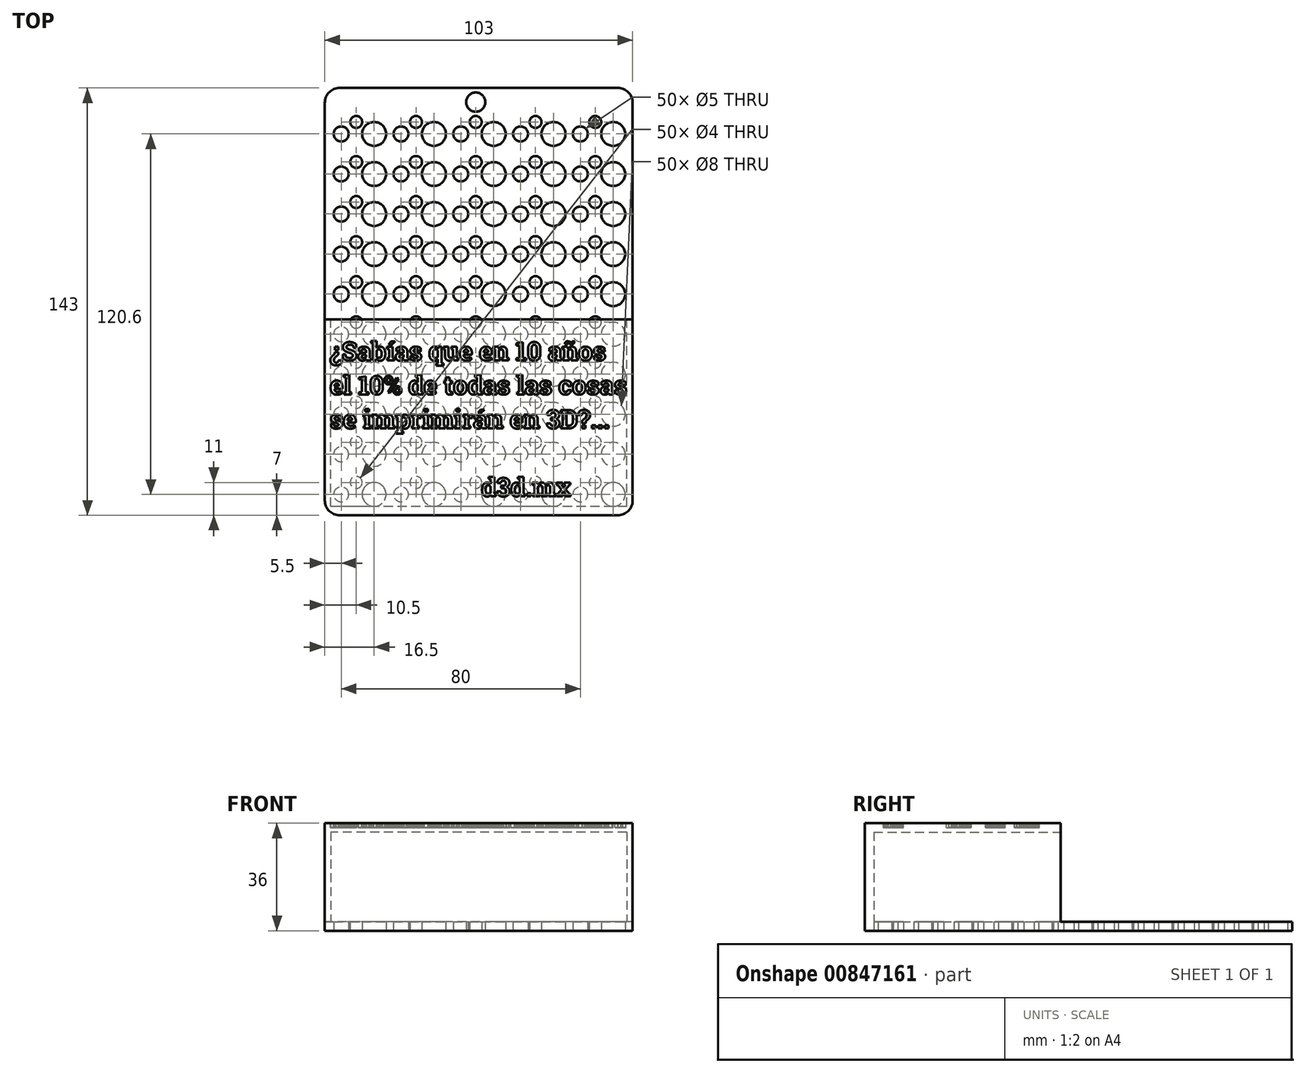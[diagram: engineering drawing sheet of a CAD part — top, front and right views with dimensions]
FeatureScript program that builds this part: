
annotation { "Feature Type Name" : "Feature", "Feature Type Description" : "" }
export const myFeature = defineFeature(function(context is Context, id is Id, definition is map)
    precondition{}
    {
        {
            var Q0;
            Q0=qCreatedBy(makeId("Top.planeOp"),FACE);
            var sketch = newSketch(context, id + "F0", { "sketchPlane" : qUnion([Q0])});
            skLineSegment(sketch, "E0.bottom", {"start": v(5, 0) * mm, "end": v(98, 0) * mm});
            skLineSegment(sketch, "E0.top", {"start": v(5, 143) * mm, "end": v(98, 143) * mm});
            skLineSegment(sketch, "E0.left", {"start": v(0, 5) * mm, "end": v(0, 138) * mm});
            skLineSegment(sketch, "E0.right", {"start": v(103, 5) * mm, "end": v(103, 138) * mm});
            skPoint(sketch, "E1.visualSharp", {"position": v(0, 143) * mm});
            skArc(sketch, "E1.filletArc", {"start": v(5, 143) * mm, "mid": v(1.46, 141.54) * mm, "end": v(0, 138) * mm});
            skPoint(sketch, "E2.visualSharp", {"position": v(103, 143) * mm});
            skArc(sketch, "E2.filletArc", {"start": v(103, 138) * mm, "mid": v(101.54, 141.54) * mm, "end": v(98, 143) * mm});
            skPoint(sketch, "E3.visualSharp", {"position": v(0, 0) * mm});
            skArc(sketch, "E3.filletArc", {"start": v(0, 5) * mm, "mid": v(1.46, 1.46) * mm, "end": v(5, 0) * mm});
            skPoint(sketch, "E4.visualSharp", {"position": v(103, 0) * mm});
            skArc(sketch, "E4.filletArc", {"start": v(98, 0) * mm, "mid": v(101.54, 1.46) * mm, "end": v(103, 5) * mm});
            skSolve(sketch);
        }
        {
            var Q0;
            Q0 = qSketchRegion(id + "F0", true);
            extrude(context, id + "F1", {"entities" : qUnion([Q0]), "depth" : 36 * mm, "offsetDistance" : 25 * mm});
        }
        {
            var Q0;
            Q0=makeQuery(id+"F1.opExtrude","SWEPT_FACE",FACE,{"disambiguationData":[OSD([sQuery(id+"F0.wireOp",EDGE,"E0.top")])]});
            var sketch = newSketch(context, id + "F2", { "sketchPlane" : qUnion([Q0])});
            skLineSegment(sketch, "E5.bottom", {"start": v(-103, 36) * mm, "end": v(0, 36) * mm});
            skLineSegment(sketch, "E5.top", {"start": v(-103, 3) * mm, "end": v(0, 3) * mm});
            skLineSegment(sketch, "E5.left", {"start": v(-103, 36) * mm, "end": v(-103, 3) * mm});
            skLineSegment(sketch, "E5.right", {"start": v(0, 36) * mm, "end": v(0, 3) * mm});
            skSolve(sketch);
        }
        {
            var Q0;
            Q0 = qSketchRegion(id + "F2", true);
            extrude(context, id + "F3", {"entities" : qUnion([Q0]), "operationType" : NewBodyOperationType.REMOVE, "oppositeDirection" : true, "depth" : 77.5 * mm, "offsetDistance" : 25 * mm});
        }
        {
            var Q0;
            Q0=makeQuery(id+"F3.boolean.opBoolean","COPY",FACE,{"derivedFrom":makeQuery(id+"F3.opExtrude","CAP_FACE",FACE,{"disambiguationData":[OSD([sQuery(id+"F2.wireOp",EDGE,"E5.bottom"),sQuery(id+"F2.wireOp",EDGE,"E5.top"),sQuery(id+"F2.wireOp",EDGE,"E5.left"),sQuery(id+"F2.wireOp",EDGE,"E5.right")])],"isStart":false})});
            var sketch = newSketch(context, id + "F4", { "sketchPlane" : qUnion([Q0])});
            skLineSegment(sketch, "E6.bottom", {"start": v(-101, 33) * mm, "end": v(-2, 33) * mm});
            skLineSegment(sketch, "E6.top", {"start": v(-101, 3) * mm, "end": v(-2, 3) * mm});
            skLineSegment(sketch, "E6.left", {"start": v(-101, 33) * mm, "end": v(-101, 3) * mm});
            skLineSegment(sketch, "E6.right", {"start": v(-2, 33) * mm, "end": v(-2, 3) * mm});
            skSolve(sketch);
        }
        {
            var Q0;
            Q0 = qSketchRegion(id + "F4", true);
            extrude(context, id + "F5", {"entities" : qUnion([Q0]), "operationType" : NewBodyOperationType.REMOVE, "oppositeDirection" : true, "depth" : 62.5 * mm, "offsetDistance" : 25 * mm});
        }
        {
            var Q0;
            Q0=makeQuery(id+"F1.opExtrude","CAP_FACE",FACE,{"disambiguationData":[OSD([sQuery(id+"F0.wireOp",EDGE,"E0.bottom"),sQuery(id+"F0.wireOp",EDGE,"E0.top"),sQuery(id+"F0.wireOp",EDGE,"E0.left"),sQuery(id+"F0.wireOp",EDGE,"E0.right"),sQuery(id+"F0.wireOp",EDGE,"E1.filletArc"),sQuery(id+"F0.wireOp",EDGE,"E2.filletArc"),sQuery(id+"F0.wireOp",EDGE,"E3.filletArc"),sQuery(id+"F0.wireOp",EDGE,"E4.filletArc")])],"isStart":false});
            var sketch = newSketch(context, id + "F6", { "sketchPlane" : qUnion([Q0])});
            skText(sketch, "E7", { "text": "¿Sabías que en 10 años\nel 10% de todas las cosas\nse imprimirán en 3D?...\n\n                        d3d.mx", "fontName": "RobotoSlab-Bold.ttf"});
            const initialGuessF6  = {"E7": [0.00164, 0.0518, 1, 0, 0.0062]};
            skSetInitialGuess(sketch, initialGuessF6);
            skSolve(sketch);
        }
        {
            var Q0;
            Q0 = qSketchRegion(id + "F6", true);
            extrude(context, id + "F7", {"entities" : qUnion([Q0]), "operationType" : NewBodyOperationType.REMOVE, "oppositeDirection" : true, "depth" : 1.5 * mm, "offsetDistance" : 25 * mm});
        }
        {
            var Q0;
            Q0=makeQuery(id+"F1.opExtrude","CAP_FACE",FACE,{"disambiguationData":[OSD([sQuery(id+"F0.wireOp",EDGE,"E0.bottom"),sQuery(id+"F0.wireOp",EDGE,"E0.top"),sQuery(id+"F0.wireOp",EDGE,"E0.left"),sQuery(id+"F0.wireOp",EDGE,"E0.right"),sQuery(id+"F0.wireOp",EDGE,"E1.filletArc"),sQuery(id+"F0.wireOp",EDGE,"E2.filletArc"),sQuery(id+"F0.wireOp",EDGE,"E3.filletArc"),sQuery(id+"F0.wireOp",EDGE,"E4.filletArc")])],"isStart":true});
            var sketch = newSketch(context, id + "F8", { "sketchPlane" : qUnion([Q0])});
            skCircle(sketch, "E8", {"center": v(5.5, -7) * mm, "radius": 2.5 * mm});
            skCircle(sketch, "E9", {"center": v(10.5, -11) * mm, "radius": 2 * mm});
            skCircle(sketch, "E10", {"center": v(16.5, -7) * mm, "radius": 4 * mm});
            skCircle(sketch, "E11.0.1.0", {"center": v(16.5, -20.4) * mm, "radius": 4 * mm});
            skCircle(sketch, "E11.0.1.1", {"center": v(10.5, -24.4) * mm, "radius": 2 * mm});
            skCircle(sketch, "E11.0.1.2", {"center": v(5.5, -20.4) * mm, "radius": 2.5 * mm});
            skCircle(sketch, "E11.0.2.0", {"center": v(16.5, -33.8) * mm, "radius": 4 * mm});
            skCircle(sketch, "E11.0.2.1", {"center": v(10.5, -37.8) * mm, "radius": 2 * mm});
            skCircle(sketch, "E11.0.2.2", {"center": v(5.5, -33.8) * mm, "radius": 2.5 * mm});
            skCircle(sketch, "E11.0.3.0", {"center": v(16.5, -47.2) * mm, "radius": 4 * mm});
            skCircle(sketch, "E11.0.3.1", {"center": v(10.5, -51.2) * mm, "radius": 2 * mm});
            skCircle(sketch, "E11.0.3.2", {"center": v(5.5, -47.2) * mm, "radius": 2.5 * mm});
            skCircle(sketch, "E11.0.4.0", {"center": v(16.5, -60.6) * mm, "radius": 4 * mm});
            skCircle(sketch, "E11.0.4.1", {"center": v(10.5, -64.6) * mm, "radius": 2 * mm});
            skCircle(sketch, "E11.0.4.2", {"center": v(5.5, -60.6) * mm, "radius": 2.5 * mm});
            skCircle(sketch, "E11.0.5.0", {"center": v(16.5, -74) * mm, "radius": 4 * mm});
            skCircle(sketch, "E11.0.5.1", {"center": v(10.5, -78) * mm, "radius": 2 * mm});
            skCircle(sketch, "E11.0.5.2", {"center": v(5.5, -74) * mm, "radius": 2.5 * mm});
            skCircle(sketch, "E11.0.6.0", {"center": v(16.5, -87.4) * mm, "radius": 4 * mm});
            skCircle(sketch, "E11.0.6.1", {"center": v(10.5, -91.4) * mm, "radius": 2 * mm});
            skCircle(sketch, "E11.0.6.2", {"center": v(5.5, -87.4) * mm, "radius": 2.5 * mm});
            skCircle(sketch, "E11.0.7.0", {"center": v(16.5, -100.8) * mm, "radius": 4 * mm});
            skCircle(sketch, "E11.0.7.1", {"center": v(10.5, -104.8) * mm, "radius": 2 * mm});
            skCircle(sketch, "E11.0.7.2", {"center": v(5.5, -100.8) * mm, "radius": 2.5 * mm});
            skCircle(sketch, "E11.0.8.0", {"center": v(16.5, -114.2) * mm, "radius": 4 * mm});
            skCircle(sketch, "E11.0.8.1", {"center": v(10.5, -118.2) * mm, "radius": 2 * mm});
            skCircle(sketch, "E11.0.8.2", {"center": v(5.5, -114.2) * mm, "radius": 2.5 * mm});
            skCircle(sketch, "E11.0.9.0", {"center": v(16.5, -127.6) * mm, "radius": 4 * mm});
            skCircle(sketch, "E11.0.9.1", {"center": v(10.5, -131.6) * mm, "radius": 2 * mm});
            skCircle(sketch, "E11.0.9.2", {"center": v(5.5, -127.6) * mm, "radius": 2.5 * mm});
            skCircle(sketch, "E11.1.0.0", {"center": v(36.5, -7) * mm, "radius": 4 * mm});
            skCircle(sketch, "E11.1.0.1", {"center": v(30.5, -11) * mm, "radius": 2 * mm});
            skCircle(sketch, "E11.1.0.2", {"center": v(25.5, -7) * mm, "radius": 2.5 * mm});
            skCircle(sketch, "E11.1.1.0", {"center": v(36.5, -20.4) * mm, "radius": 4 * mm});
            skCircle(sketch, "E11.1.1.1", {"center": v(30.5, -24.4) * mm, "radius": 2 * mm});
            skCircle(sketch, "E11.1.1.2", {"center": v(25.5, -20.4) * mm, "radius": 2.5 * mm});
            skCircle(sketch, "E11.1.2.0", {"center": v(36.5, -33.8) * mm, "radius": 4 * mm});
            skCircle(sketch, "E11.1.2.1", {"center": v(30.5, -37.8) * mm, "radius": 2 * mm});
            skCircle(sketch, "E11.1.2.2", {"center": v(25.5, -33.8) * mm, "radius": 2.5 * mm});
            skCircle(sketch, "E11.1.3.0", {"center": v(36.5, -47.2) * mm, "radius": 4 * mm});
            skCircle(sketch, "E11.1.3.1", {"center": v(30.5, -51.2) * mm, "radius": 2 * mm});
            skCircle(sketch, "E11.1.3.2", {"center": v(25.5, -47.2) * mm, "radius": 2.5 * mm});
            skCircle(sketch, "E11.1.4.0", {"center": v(36.5, -60.6) * mm, "radius": 4 * mm});
            skCircle(sketch, "E11.1.4.1", {"center": v(30.5, -64.6) * mm, "radius": 2 * mm});
            skCircle(sketch, "E11.1.4.2", {"center": v(25.5, -60.6) * mm, "radius": 2.5 * mm});
            skCircle(sketch, "E11.1.5.0", {"center": v(36.5, -74) * mm, "radius": 4 * mm});
            skCircle(sketch, "E11.1.5.1", {"center": v(30.5, -78) * mm, "radius": 2 * mm});
            skCircle(sketch, "E11.1.5.2", {"center": v(25.5, -74) * mm, "radius": 2.5 * mm});
            skCircle(sketch, "E11.1.6.0", {"center": v(36.5, -87.4) * mm, "radius": 4 * mm});
            skCircle(sketch, "E11.1.6.1", {"center": v(30.5, -91.4) * mm, "radius": 2 * mm});
            skCircle(sketch, "E11.1.6.2", {"center": v(25.5, -87.4) * mm, "radius": 2.5 * mm});
            skCircle(sketch, "E11.1.7.0", {"center": v(36.5, -100.8) * mm, "radius": 4 * mm});
            skCircle(sketch, "E11.1.7.1", {"center": v(30.5, -104.8) * mm, "radius": 2 * mm});
            skCircle(sketch, "E11.1.7.2", {"center": v(25.5, -100.8) * mm, "radius": 2.5 * mm});
            skCircle(sketch, "E11.1.8.0", {"center": v(36.5, -114.2) * mm, "radius": 4 * mm});
            skCircle(sketch, "E11.1.8.1", {"center": v(30.5, -118.2) * mm, "radius": 2 * mm});
            skCircle(sketch, "E11.1.8.2", {"center": v(25.5, -114.2) * mm, "radius": 2.5 * mm});
            skCircle(sketch, "E11.1.9.0", {"center": v(36.5, -127.6) * mm, "radius": 4 * mm});
            skCircle(sketch, "E11.1.9.1", {"center": v(30.5, -131.6) * mm, "radius": 2 * mm});
            skCircle(sketch, "E11.1.9.2", {"center": v(25.5, -127.6) * mm, "radius": 2.5 * mm});
            skCircle(sketch, "E11.2.0.0", {"center": v(56.5, -7) * mm, "radius": 4 * mm});
            skCircle(sketch, "E11.2.0.1", {"center": v(50.5, -11) * mm, "radius": 2 * mm});
            skCircle(sketch, "E11.2.0.2", {"center": v(45.5, -7) * mm, "radius": 2.5 * mm});
            skCircle(sketch, "E11.2.1.0", {"center": v(56.5, -20.4) * mm, "radius": 4 * mm});
            skCircle(sketch, "E11.2.1.1", {"center": v(50.5, -24.4) * mm, "radius": 2 * mm});
            skCircle(sketch, "E11.2.1.2", {"center": v(45.5, -20.4) * mm, "radius": 2.5 * mm});
            skCircle(sketch, "E11.2.2.0", {"center": v(56.5, -33.8) * mm, "radius": 4 * mm});
            skCircle(sketch, "E11.2.2.1", {"center": v(50.5, -37.8) * mm, "radius": 2 * mm});
            skCircle(sketch, "E11.2.2.2", {"center": v(45.5, -33.8) * mm, "radius": 2.5 * mm});
            skCircle(sketch, "E11.2.3.0", {"center": v(56.5, -47.2) * mm, "radius": 4 * mm});
            skCircle(sketch, "E11.2.3.1", {"center": v(50.5, -51.2) * mm, "radius": 2 * mm});
            skCircle(sketch, "E11.2.3.2", {"center": v(45.5, -47.2) * mm, "radius": 2.5 * mm});
            skCircle(sketch, "E11.2.4.0", {"center": v(56.5, -60.6) * mm, "radius": 4 * mm});
            skCircle(sketch, "E11.2.4.1", {"center": v(50.5, -64.6) * mm, "radius": 2 * mm});
            skCircle(sketch, "E11.2.4.2", {"center": v(45.5, -60.6) * mm, "radius": 2.5 * mm});
            skCircle(sketch, "E11.2.5.0", {"center": v(56.5, -74) * mm, "radius": 4 * mm});
            skCircle(sketch, "E11.2.5.1", {"center": v(50.5, -78) * mm, "radius": 2 * mm});
            skCircle(sketch, "E11.2.5.2", {"center": v(45.5, -74) * mm, "radius": 2.5 * mm});
            skCircle(sketch, "E11.2.6.0", {"center": v(56.5, -87.4) * mm, "radius": 4 * mm});
            skCircle(sketch, "E11.2.6.1", {"center": v(50.5, -91.4) * mm, "radius": 2 * mm});
            skCircle(sketch, "E11.2.6.2", {"center": v(45.5, -87.4) * mm, "radius": 2.5 * mm});
            skCircle(sketch, "E11.2.7.0", {"center": v(56.5, -100.8) * mm, "radius": 4 * mm});
            skCircle(sketch, "E11.2.7.1", {"center": v(50.5, -104.8) * mm, "radius": 2 * mm});
            skCircle(sketch, "E11.2.7.2", {"center": v(45.5, -100.8) * mm, "radius": 2.5 * mm});
            skCircle(sketch, "E11.2.8.0", {"center": v(56.5, -114.2) * mm, "radius": 4 * mm});
            skCircle(sketch, "E11.2.8.1", {"center": v(50.5, -118.2) * mm, "radius": 2 * mm});
            skCircle(sketch, "E11.2.8.2", {"center": v(45.5, -114.2) * mm, "radius": 2.5 * mm});
            skCircle(sketch, "E11.2.9.0", {"center": v(56.5, -127.6) * mm, "radius": 4 * mm});
            skCircle(sketch, "E11.2.9.1", {"center": v(50.5, -131.6) * mm, "radius": 2 * mm});
            skCircle(sketch, "E11.2.9.2", {"center": v(45.5, -127.6) * mm, "radius": 2.5 * mm});
            skCircle(sketch, "E11.3.0.0", {"center": v(76.5, -7) * mm, "radius": 4 * mm});
            skCircle(sketch, "E11.3.0.1", {"center": v(70.5, -11) * mm, "radius": 2 * mm});
            skCircle(sketch, "E11.3.0.2", {"center": v(65.5, -7) * mm, "radius": 2.5 * mm});
            skCircle(sketch, "E11.3.1.0", {"center": v(76.5, -20.4) * mm, "radius": 4 * mm});
            skCircle(sketch, "E11.3.1.1", {"center": v(70.5, -24.4) * mm, "radius": 2 * mm});
            skCircle(sketch, "E11.3.1.2", {"center": v(65.5, -20.4) * mm, "radius": 2.5 * mm});
            skCircle(sketch, "E11.3.2.0", {"center": v(76.5, -33.8) * mm, "radius": 4 * mm});
            skCircle(sketch, "E11.3.2.1", {"center": v(70.5, -37.8) * mm, "radius": 2 * mm});
            skCircle(sketch, "E11.3.2.2", {"center": v(65.5, -33.8) * mm, "radius": 2.5 * mm});
            skCircle(sketch, "E11.3.3.0", {"center": v(76.5, -47.2) * mm, "radius": 4 * mm});
            skCircle(sketch, "E11.3.3.1", {"center": v(70.5, -51.2) * mm, "radius": 2 * mm});
            skCircle(sketch, "E11.3.3.2", {"center": v(65.5, -47.2) * mm, "radius": 2.5 * mm});
            skCircle(sketch, "E11.3.4.0", {"center": v(76.5, -60.6) * mm, "radius": 4 * mm});
            skCircle(sketch, "E11.3.4.1", {"center": v(70.5, -64.6) * mm, "radius": 2 * mm});
            skCircle(sketch, "E11.3.4.2", {"center": v(65.5, -60.6) * mm, "radius": 2.5 * mm});
            skCircle(sketch, "E11.3.5.0", {"center": v(76.5, -74) * mm, "radius": 4 * mm});
            skCircle(sketch, "E11.3.5.1", {"center": v(70.5, -78) * mm, "radius": 2 * mm});
            skCircle(sketch, "E11.3.5.2", {"center": v(65.5, -74) * mm, "radius": 2.5 * mm});
            skCircle(sketch, "E11.3.6.0", {"center": v(76.5, -87.4) * mm, "radius": 4 * mm});
            skCircle(sketch, "E11.3.6.1", {"center": v(70.5, -91.4) * mm, "radius": 2 * mm});
            skCircle(sketch, "E11.3.6.2", {"center": v(65.5, -87.4) * mm, "radius": 2.5 * mm});
            skCircle(sketch, "E11.3.7.0", {"center": v(76.5, -100.8) * mm, "radius": 4 * mm});
            skCircle(sketch, "E11.3.7.1", {"center": v(70.5, -104.8) * mm, "radius": 2 * mm});
            skCircle(sketch, "E11.3.7.2", {"center": v(65.5, -100.8) * mm, "radius": 2.5 * mm});
            skCircle(sketch, "E11.3.8.0", {"center": v(76.5, -114.2) * mm, "radius": 4 * mm});
            skCircle(sketch, "E11.3.8.1", {"center": v(70.5, -118.2) * mm, "radius": 2 * mm});
            skCircle(sketch, "E11.3.8.2", {"center": v(65.5, -114.2) * mm, "radius": 2.5 * mm});
            skCircle(sketch, "E11.3.9.0", {"center": v(76.5, -127.6) * mm, "radius": 4 * mm});
            skCircle(sketch, "E11.3.9.1", {"center": v(70.5, -131.6) * mm, "radius": 2 * mm});
            skCircle(sketch, "E11.3.9.2", {"center": v(65.5, -127.6) * mm, "radius": 2.5 * mm});
            skCircle(sketch, "E11.4.0.0", {"center": v(96.5, -7) * mm, "radius": 4 * mm});
            skCircle(sketch, "E11.4.0.1", {"center": v(90.5, -11) * mm, "radius": 2 * mm});
            skCircle(sketch, "E11.4.0.2", {"center": v(85.5, -7) * mm, "radius": 2.5 * mm});
            skCircle(sketch, "E11.4.1.0", {"center": v(96.5, -20.4) * mm, "radius": 4 * mm});
            skCircle(sketch, "E11.4.1.1", {"center": v(90.5, -24.4) * mm, "radius": 2 * mm});
            skCircle(sketch, "E11.4.1.2", {"center": v(85.5, -20.4) * mm, "radius": 2.5 * mm});
            skCircle(sketch, "E11.4.2.0", {"center": v(96.5, -33.8) * mm, "radius": 4 * mm});
            skCircle(sketch, "E11.4.2.1", {"center": v(90.5, -37.8) * mm, "radius": 2 * mm});
            skCircle(sketch, "E11.4.2.2", {"center": v(85.5, -33.8) * mm, "radius": 2.5 * mm});
            skCircle(sketch, "E11.4.3.0", {"center": v(96.5, -47.2) * mm, "radius": 4 * mm});
            skCircle(sketch, "E11.4.3.1", {"center": v(90.5, -51.2) * mm, "radius": 2 * mm});
            skCircle(sketch, "E11.4.3.2", {"center": v(85.5, -47.2) * mm, "radius": 2.5 * mm});
            skCircle(sketch, "E11.4.4.0", {"center": v(96.5, -60.6) * mm, "radius": 4 * mm});
            skCircle(sketch, "E11.4.4.1", {"center": v(90.5, -64.6) * mm, "radius": 2 * mm});
            skCircle(sketch, "E11.4.4.2", {"center": v(85.5, -60.6) * mm, "radius": 2.5 * mm});
            skCircle(sketch, "E11.4.5.0", {"center": v(96.5, -74) * mm, "radius": 4 * mm});
            skCircle(sketch, "E11.4.5.1", {"center": v(90.5, -78) * mm, "radius": 2 * mm});
            skCircle(sketch, "E11.4.5.2", {"center": v(85.5, -74) * mm, "radius": 2.5 * mm});
            skCircle(sketch, "E11.4.6.0", {"center": v(96.5, -87.4) * mm, "radius": 4 * mm});
            skCircle(sketch, "E11.4.6.1", {"center": v(90.5, -91.4) * mm, "radius": 2 * mm});
            skCircle(sketch, "E11.4.6.2", {"center": v(85.5, -87.4) * mm, "radius": 2.5 * mm});
            skCircle(sketch, "E11.4.7.0", {"center": v(96.5, -100.8) * mm, "radius": 4 * mm});
            skCircle(sketch, "E11.4.7.1", {"center": v(90.5, -104.8) * mm, "radius": 2 * mm});
            skCircle(sketch, "E11.4.7.2", {"center": v(85.5, -100.8) * mm, "radius": 2.5 * mm});
            skCircle(sketch, "E11.4.8.0", {"center": v(96.5, -114.2) * mm, "radius": 4 * mm});
            skCircle(sketch, "E11.4.8.1", {"center": v(90.5, -118.2) * mm, "radius": 2 * mm});
            skCircle(sketch, "E11.4.8.2", {"center": v(85.5, -114.2) * mm, "radius": 2.5 * mm});
            skCircle(sketch, "E11.4.9.0", {"center": v(96.5, -127.6) * mm, "radius": 4 * mm});
            skCircle(sketch, "E11.4.9.1", {"center": v(90.5, -131.6) * mm, "radius": 2 * mm});
            skCircle(sketch, "E11.4.9.2", {"center": v(85.5, -127.6) * mm, "radius": 2.5 * mm});
            skLineSegment(sketch, "E11.direction1", {"start": v(5.5, -7) * mm, "end": v(25.5, -7) * mm, "construction": true});
            skLineSegment(sketch, "E11.direction2", {"start": v(5.5, -7) * mm, "end": v(5.5, -20.4) * mm, "construction": true});
            skCircle(sketch, "E12", {"center": v(50.5, -138.24) * mm, "radius": 3.2 * mm});
            skSolve(sketch);
        }
        {
            var Q0;
            Q0 = qSketchRegion(id + "F8", true);
            extrude(context, id + "F9", {"entities" : qUnion([Q0]), "operationType" : NewBodyOperationType.REMOVE, "endBound" : BoundingType.UP_TO_NEXT, "oppositeDirection" : true, "depth" : 25 * mm, "offsetDistance" : 25 * mm});
        }
    });
